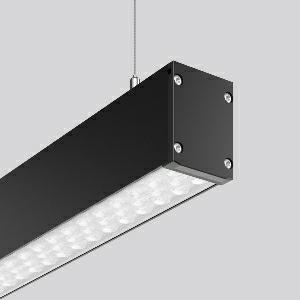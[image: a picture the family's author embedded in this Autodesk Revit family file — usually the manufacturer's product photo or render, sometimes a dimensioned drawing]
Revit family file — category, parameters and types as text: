
# Revit family: linedo_single_ip54_312565_003_76_6130
name_source: partatom
category: Lighting Fixtures
units: mm (PartAtom-declared; Revit-internal decimal feet)

## family parameters
Cut with Voids When Loaded = No
Host = Face
Light Source = No
Part Type = Normal
Room Calculation Point = No
Round Connector Dimension = Use Diameter
Shared = No

## types (1)
- LINEDO single IP54 (1 x LED Modul 830, 4550 lm, 3000)
    Apparent Load = 31 VA
    CIE Flux Codes = 86 96 99 100 100
    Color Rendering = 80
    Color Temperature = 3000
    Default Elevation = 1800 mm
    Description = Series: LINEDO single IP54
Stylish pendant luminaire. Housing: extruded aluminium profile, powder-coated. Plastic end caps, black. High-efficiency LED units with optimum light control thanks to clear plastic (PC) lens optics. 2-point steel cable suspension freely positionable and infinitely height-adjustable. With power cord (2.5 m). Please order canopy separately if required. Perfect for office areas (RUG < 19) and environments with computer screens in accordance with EN 12464-1. Luminaire with limited surface temperature in accordance with EN 60598-2-24 for use in environments in which a deposit of conductive dust on the luminaire can be expected. 
Colour: jet black (RAL 9005)
Length: 1710 mm
Width: 58 mm
Height: 76 mm
Suspension length: 100-1500 mm
Lamp: LED
Socket: without socket
Colour temperature: 3000K
Colour rendering index (CRI): 80
System power: 31 W
Rated luminous flux: 4550 lm
Beam angle Down: 59°
Luminous efficiency: 147 lm/W
Control gear: Converter, dimmable, DALI
Protection class: I
Type of protection: IP 54
    Height = 76 mm
    Lamp = 1 x LED Modul 830
    Lamp Light Flux = 4550 lm
    Lamp count = 1
    Length = 1710 mm
    Lifetime = 50000 h
    Luminous efficacy = 147 lm/W
    Manufacturer = RZB
    ModVariant = No
    Model = 312565.003.76
    Mounting Place = Ceiling
    Mounting Type = Surface mounted, Pendant
    Number of Poles = 1
    OnlyDefault = Yes
    Power Factor = 1
    Product Name = LINEDO single IP54
    Product group = Pendant luminaires
    ProductGroupID = 902
    Protection Class = Protection class I
    Protection Degree = IP 54
    RLX_Detail_Level = 1
    RLX_Emergency_Light_Flux = 0 lm
    RLX_Emergency_Type = 0
    RLX_Emergency_Type_DB = No
    RlxData = <blob elided: 35953 chars, md5=e23d2604>
    Socket = socket
    Standby Power = 0 W
    System Light Flux = 4550 lm
    System Power = 31 W
    Type Comments = ALEA SPOT
    Type Image = 312565.003.jpg
    URL = http://relux.com
    VarID = ---
    Voltage = 230 V
    Voltage Range = 220-240 V
    Weight = 0.00 kg
    Width = 58 mm

## geometry (parser evidence)
native form markers: Blend x4, Sweep x10
no freeform markers — native parametric forms only
